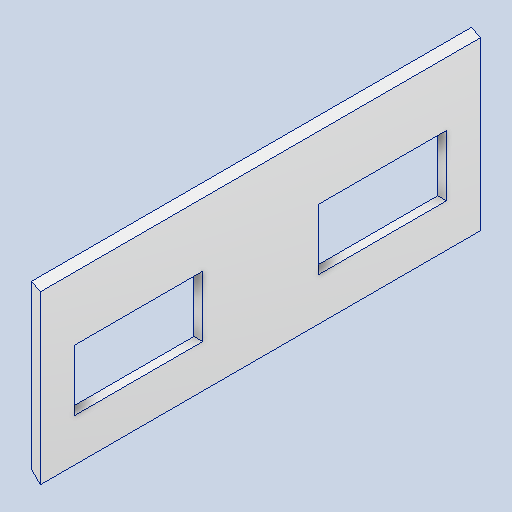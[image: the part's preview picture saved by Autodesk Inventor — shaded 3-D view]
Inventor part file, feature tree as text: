
AUTODESK INVENTOR PART (.ipt)
format: ipt  version: 2023 (Build 270158000, 158)  size: 162,304 bytes
history: native  units: mm
features: other x3, extrude x3, sketch x3, chamfer x1, reference x1
ambient origin geometry x8: Origin, YZ Plane, XZ Plane, XY Plane, X Axis, Y Axis, Z Axis, Center Point
bodies: Body1 (feature_tree)
feature tree (11):
  other  "Bryła1"
  extrude  "Wyciągnięcie proste1"  Depth=2.0mm TaperAngle=0.0deg
  chamfer  "Faza1"  Distance=2.0mm Angle=45.0deg
  extrude  "Wyciągnięcie proste2"  TaperAngle=0.0deg  [1 undecoded]
  extrude  "Wyciągnięcie proste3"  Depth=2.0mm
  sketch  "Szkic1"
  sketch  "Szkic2"
  reference  "Odniesienie1"
  sketch  "Szkic3"
  other  "Zespół1"
  other  "sciana_prawa_nowa:1"
note: 1 required parameter value undecoded (feature->parameter linkage not recoverable at this tier; creation-order binding heuristic only, values carry confidence <= 0.55)
